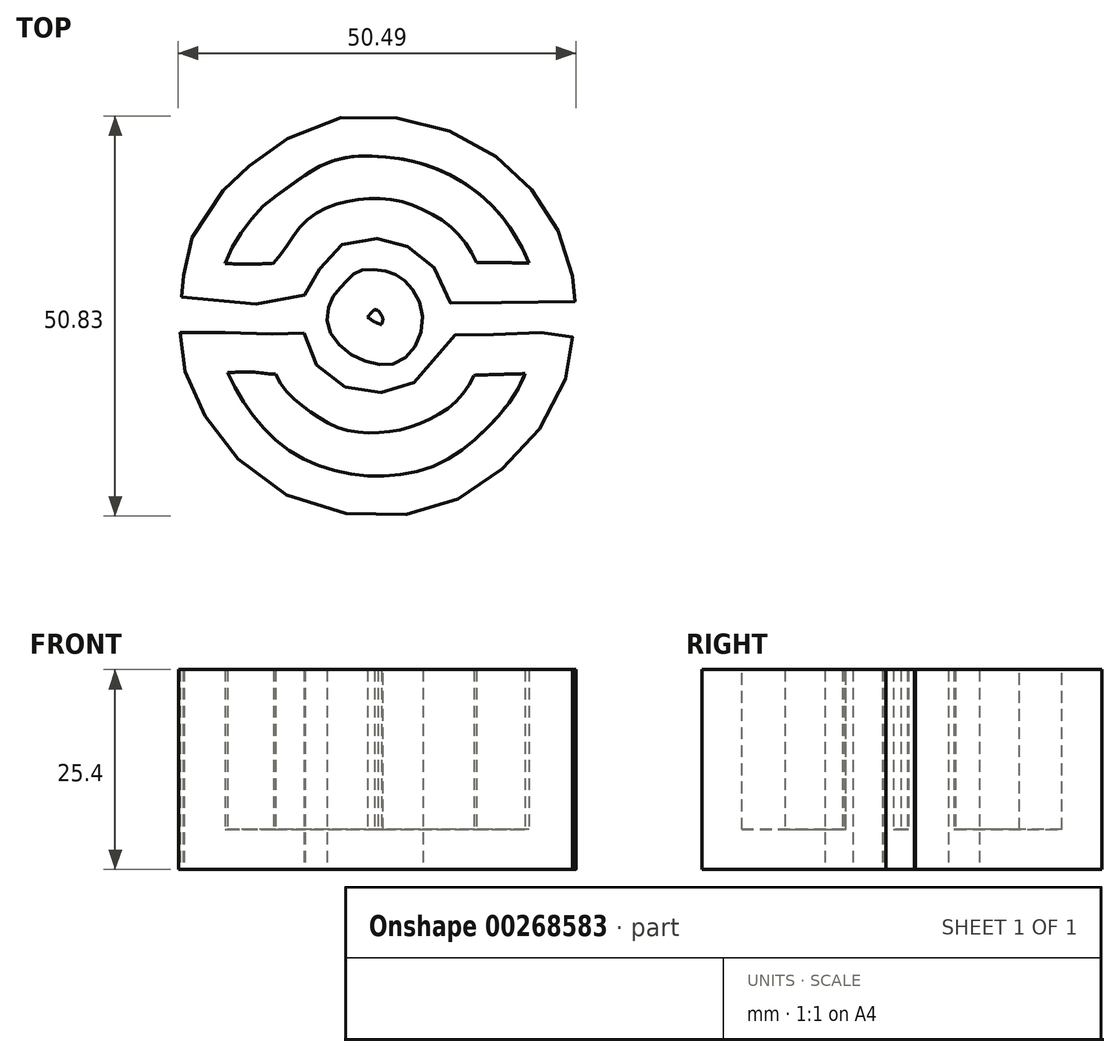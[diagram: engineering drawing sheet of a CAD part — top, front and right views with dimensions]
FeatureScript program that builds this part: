
annotation { "Feature Type Name" : "Feature", "Feature Type Description" : "" }
export const myFeature = defineFeature(function(context is Context, id is Id, definition is map)
    precondition{}
    {
        {
            var Q0;
            Q0=qCreatedBy(makeId("Top.planeOp"),FACE);
            var sketch = newSketch(context, id + "F0", { "sketchPlane" : qUnion([Q0])});
            skFitSpline(sketch, "E0", {"points": [v(-23, -10.62) * mm, v(-22.02, -13.69) * mm, v(-19.29, -16.42) * mm, v(-16.55, -17.96) * mm, v(-12.5, -18.07) * mm, v(-9.44, -17.08) * mm, v(-6.37, -14.56) * mm, v(-4.84, -10.84) * mm, v(-3.86, -10.84) * mm, v(0, -10.84) * mm, v(6.1, -10.62) * mm, v(10.7, -10.62) * mm, v(11.13, -11.6) * mm, v(9.6, -18.18) * mm, v(4.68, -25.4) * mm, v(-1.56, -30.65) * mm, v(-9.1, -33.5) * mm, v(-19.18, -33.28) * mm, v(-28.92, -28.9) * mm, v(-34.94, -22.12) * mm, v(-37.9, -16.2) * mm, v(-38.87, -10.73) * mm, v(-37.78, -10.62) * mm, v(-29.03, -10.52) * mm, v(-26.07, -10.73) * mm, v(-23, -10.62) * mm]});
            skFitSpline(sketch, "E1", {"points": [v(-38.55, -6.03) * mm, v(-23, -6.25) * mm, v(-23, -5.48) * mm, v(-21.26, -2.86) * mm, v(-19.18, 0) * mm, v(-15.46, 1.3) * mm, v(-12.06, 1.2) * mm, v(-9.1, 0) * mm, v(-6.26, -2.64) * mm, v(-4.4, -6.8) * mm, v(-3.97, -6.8) * mm, v(11.46, -6.58) * mm, v(11.35, -6.14) * mm, v(11.03, -2.42) * mm, v(7.96, 4.7) * mm, v(3.58, 10.06) * mm, v(-3.53, 14.65) * mm, v(-12.4, 16.84) * mm, v(-22.13, 15.64) * mm, v(-29.46, 10.93) * mm, v(-31.76, 9.18) * mm, v(-36.9, 2.07) * mm, v(-38.33, -2.96) * mm, v(-38.33, -4.83) * mm, v(-38.55, -6.03) * mm]});
            skFitSpline(sketch, "E2", {"points": [v(-19.62, -10.62) * mm, v(-19.62, -6.58) * mm, v(-17.65, -4.06) * mm, v(-16, -2.75) * mm, v(-12.61, -2.75) * mm, v(-9.99, -4.17) * mm, v(-7.9, -8.66) * mm, v(-10.31, -13.9) * mm, v(-15.13, -14.24) * mm, v(-19.62, -10.62) * mm]});
            skSolve(sketch);
        }
        {
            var Q0;
            Q0=makeQuery(id+"F0.imprint","IMPRINT",FACE,{"disambiguationData":[TD([[makeQuery(id+"F0.imprint","IMPRINT",EDGE,{"derivedFrom":sQuery(id+"F0.wireOp",EDGE,"E1")}),1.0]])]});
            var Q1;
            Q1=makeQuery(id+"F0.imprint","IMPRINT",FACE,{"disambiguationData":[TD([[makeQuery(id+"F0.imprint","IMPRINT",EDGE,{"derivedFrom":sQuery(id+"F0.wireOp",EDGE,"E2")}),-1.0]])]});
            var Q2;
            Q2=makeQuery(id+"F0.imprint","IMPRINT",FACE,{"disambiguationData":[TD([[makeQuery(id+"F0.imprint","IMPRINT",EDGE,{"derivedFrom":sQuery(id+"F0.wireOp",EDGE,"E0")}),-1.0]])]});
            extrude(context, id + "F1", {"entities" : qUnion([Q0, Q1, Q2]), "depth" : 25.4 * mm});
        }
        {
            var Q0;
            Q0=makeQuery(id+"F1.opExtrude","CAP_FACE",FACE,{"disambiguationData":[OSD([sQuery(id+"F0.wireOp",EDGE,"E0")])],"isStart":false});
            var Q1;
            Q1=makeQuery(id+"F1.opExtrude","CAP_FACE",FACE,{"disambiguationData":[OSD([sQuery(id+"F0.wireOp",EDGE,"E2")])],"isStart":false});
            var Q2;
            Q2=makeQuery(id+"F1.opExtrude","CAP_FACE",FACE,{"disambiguationData":[OSD([sQuery(id+"F0.wireOp",EDGE,"E1")])],"isStart":false});
            shell(context, id + "F2", {"entities" : qUnion([Q0, Q1, Q2]), "thickness" : 5.08 * mm});
        }
    });
